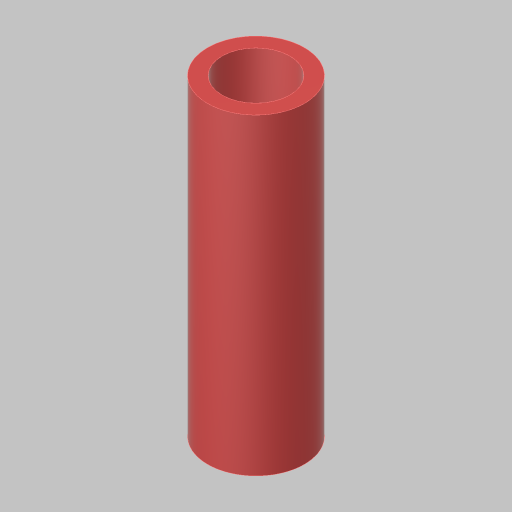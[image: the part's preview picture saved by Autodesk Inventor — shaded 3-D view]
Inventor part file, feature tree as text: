
AUTODESK INVENTOR PART (.ipt)
format: ipt  version: 2023.5 (Build 275446000, 446)  size: 103,936 bytes
history: native  units: in
note: dims shown in document units (in); Inventor stores cm internally (conversion verified against a paired STEP export)
features: extrude x1, sketch x1
ambient origin geometry x8: Origin, YZ Plane, XZ Plane, XY Plane, X Axis, Y Axis, Z Axis, Center Point
bodies: Solid1 (feature_tree)
feature tree (2):
  extrude  "Extrusion1"  Depth=2.68in
  sketch  "Sketch1"  dims[d0=0.58in d1=0.125in d2=2.68in d3=0.0in]
